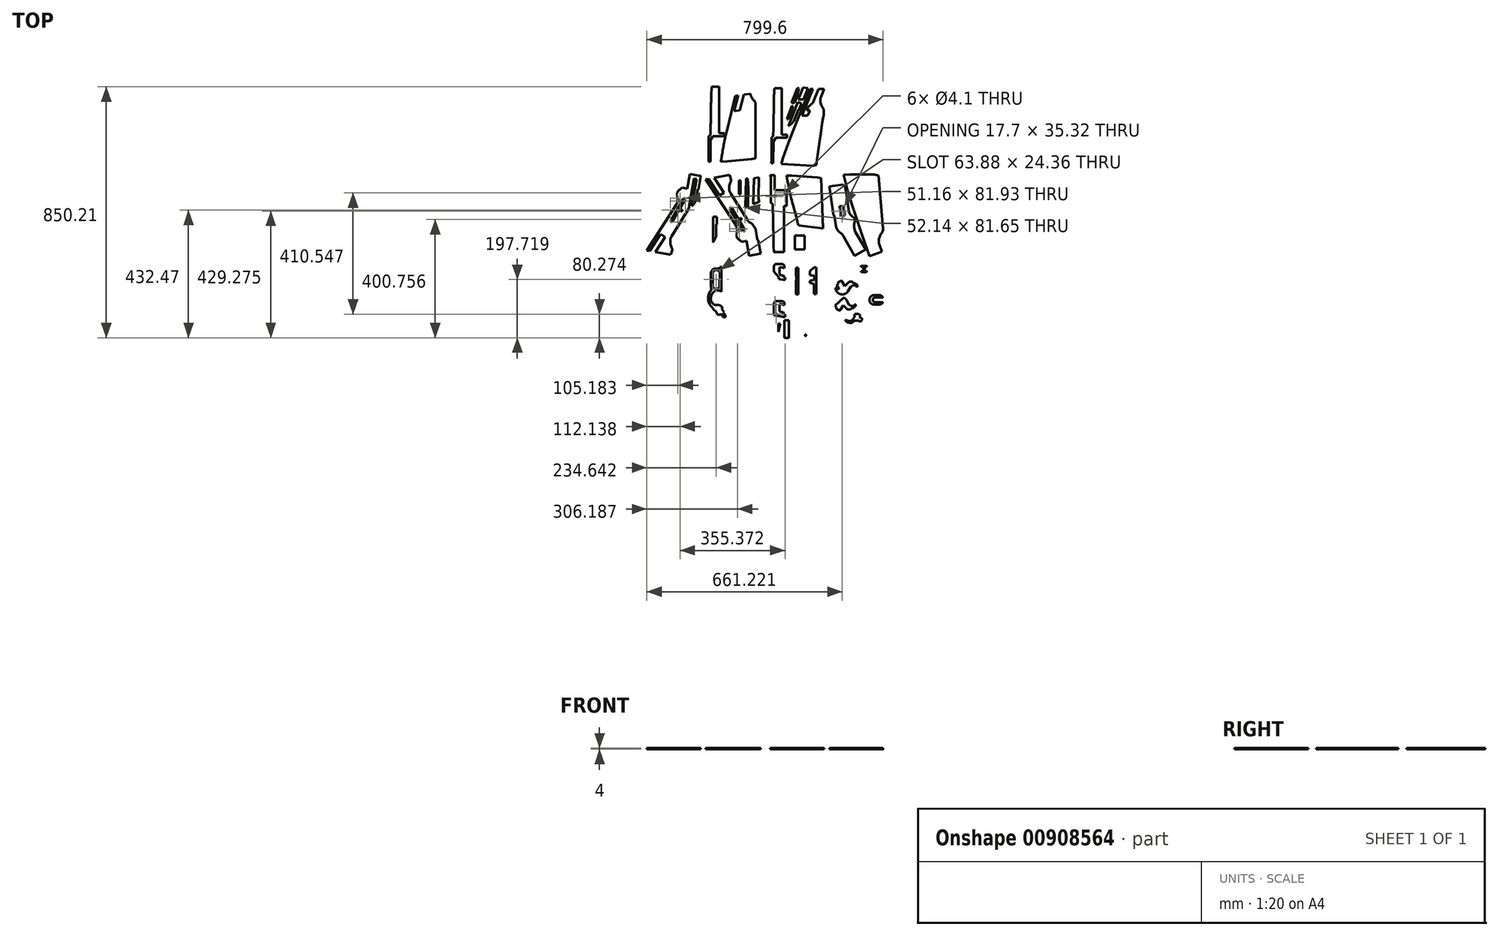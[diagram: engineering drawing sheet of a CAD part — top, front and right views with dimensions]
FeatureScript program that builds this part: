
annotation { "Feature Type Name" : "Feature", "Feature Type Description" : "" }
export const myFeature = defineFeature(function(context is Context, id is Id, definition is map)
    precondition{}
    {
        {
            var Q0;
            Q0=qCreatedBy(makeId("Top.planeOp"),FACE);
            var sketch = newSketch(context, id + "F0", { "sketchPlane" : qUnion([Q0])});
            skLineSegment(sketch, "E0", {"start": v(-149.17, 147.65) * mm, "end": v(-126.87, 148.64) * mm});
            skLineSegment(sketch, "E1", {"start": v(-126.87, 148.64) * mm, "end": v(-45.65, 148.64) * mm});
            skLineSegment(sketch, "E2", {"start": v(-45.65, 148.64) * mm, "end": v(-31.11, 145.65) * mm});
            skLineSegment(sketch, "E3", {"start": v(-31.11, 145.65) * mm, "end": v(-16.66, -19.3) * mm});
            skLineSegment(sketch, "E4", {"start": v(-149.17, 147.65) * mm, "end": v(-134.77, 92.63) * mm});
            skLineSegment(sketch, "E5", {"start": v(-134.77, 92.63) * mm, "end": v(-120.01, 43.25) * mm});
            skLineSegment(sketch, "E6", {"start": v(-120.01, 43.25) * mm, "end": v(-84.94, -59.33) * mm});
            skLineSegment(sketch, "E7", {"start": v(-84.94, -59.33) * mm, "end": v(-61, -127.23) * mm});
            skLineSegment(sketch, "E8", {"start": v(-61, -127.23) * mm, "end": v(-19.3, -112.53) * mm});
            skLineSegment(sketch, "E9", {"start": v(-19.3, -112.53) * mm, "end": v(-28.25, -87.13) * mm});
            skFitSpline(sketch, "E10", {"points": [v(-28.25, -87.13) * mm, v(-29.8, -80.26) * mm, v(-30, -73.96) * mm, v(-28.25, -65.46) * mm, v(-24.65, -56.16) * mm, v(-21.41, -51.03) * mm, v(-17.98, -46.65) * mm, v(-16.48, -43.2) * mm, v(-15.7, -38.91) * mm, v(-15.5, -33.52) * mm, v(-16.66, -19.3) * mm], "startDerivative": vector(-18, 68.99) * mm, "endDerivative": vector(-10.86, 110.65) * mm});
            skLineSegment(sketch, "E11", {"start": v(-196.66, 108.69) * mm, "end": v(-150.29, 115.09) * mm});
            skLineSegment(sketch, "E12", {"start": v(-150.29, 115.09) * mm, "end": v(-149.74, 111.15) * mm});
            skLineSegment(sketch, "E13", {"start": v(-196.66, 108.69) * mm, "end": v(-182.68, 10.6) * mm});
            skLineSegment(sketch, "E14", {"start": v(-182.68, 10.6) * mm, "end": v(-180.62, 10.89) * mm});
            skLineSegment(sketch, "E15", {"start": v(-180.62, 10.89) * mm, "end": v(-174.86, -29.47) * mm});
            skLineSegment(sketch, "E16", {"start": v(-174.86, -29.47) * mm, "end": v(-170.39, -37.35) * mm});
            skFitSpline(sketch, "E17", {"points": [v(-170.39, -37.35) * mm, v(-167.86, -41.24) * mm, v(-164.52, -45.04) * mm, v(-161.57, -47.92) * mm, v(-158, -49.98) * mm, v(-155.75, -51.53) * mm, v(-152.83, -54.2) * mm, v(-149.96, -58.52) * mm], "startDerivative": vector(15.54, -26.2) * mm, "endDerivative": vector(17.07, -29.01) * mm});
            skLineSegment(sketch, "E18", {"start": v(-149.96, -58.52) * mm, "end": v(-111.45, -126.79) * mm});
            skLineSegment(sketch, "E19", {"start": v(-111.45, -126.79) * mm, "end": v(-73.88, -104.23) * mm});
            skLineSegment(sketch, "E20", {"start": v(-73.88, -104.23) * mm, "end": v(-109.1, -45.56) * mm});
            skFitSpline(sketch, "E21", {"points": [v(-109.1, -45.56) * mm, v(-110.9, -40.12) * mm, v(-112.61, -33.86) * mm, v(-113.49, -27.7) * mm, v(-113.05, -20.62) * mm, v(-111.3, -12.06) * mm, v(-110.96, -7.06) * mm, v(-111.46, -2.22) * mm, v(-112.17, 0) * mm, v(-114.15, 2.77) * mm, v(-117.22, 5.63) * mm, v(-122.88, 9.97) * mm, v(-126.73, 13.7) * mm, v(-129.53, 18.43) * mm, v(-132.33, 32.32) * mm, v(-135.24, 52.15) * mm, v(-140.51, 88.4) * mm, v(-143.26, 106.36) * mm], "startDerivative": vector(-37.16, 108.53) * mm, "endDerivative": vector(-28.2, 180.9) * mm});
            skFitSpline(sketch, "E22", {"points": [v(-143.26, 106.36) * mm, v(-144.53, 106.7) * mm, v(-146.82, 107.98) * mm, v(-148.38, 109.32) * mm, v(-149.74, 111.15) * mm], "startDerivative": vector(-5.84, 1.08) * mm, "endDerivative": vector(-5.05, 7.35) * mm});
            skLineSegment(sketch, "E23", {"start": v(-162.7, 40.87) * mm, "end": v(-148.72, 42.74) * mm});
            skLineSegment(sketch, "E24.bottom", {"start": v(-314.34, -57.8) * mm, "end": v(-280.77, -57.8) * mm});
            skLineSegment(sketch, "E24.top", {"start": v(-314.34, -104.97) * mm, "end": v(-280.77, -104.97) * mm});
            skLineSegment(sketch, "E24.left", {"start": v(-314.34, -57.8) * mm, "end": v(-314.34, -104.97) * mm});
            skLineSegment(sketch, "E24.right", {"start": v(-280.77, -57.8) * mm, "end": v(-280.77, -104.97) * mm});
            skLineSegment(sketch, "E25", {"start": v(-383, 146.15) * mm, "end": v(-383, 95.33) * mm});
            skLineSegment(sketch, "E26", {"start": v(-383, 95.33) * mm, "end": v(-342.44, 95.33) * mm});
            skLineSegment(sketch, "E27", {"start": v(-342.44, 95.33) * mm, "end": v(-342.44, 43.12) * mm});
            skLineSegment(sketch, "E28", {"start": v(-342.44, 43.12) * mm, "end": v(-351.35, 43.12) * mm});
            skLineSegment(sketch, "E29", {"start": v(-351.35, 43.12) * mm, "end": v(-351.35, -114.1) * mm});
            skLineSegment(sketch, "E30", {"start": v(-351.35, -114.1) * mm, "end": v(-384.8, -114.1) * mm});
            skLineSegment(sketch, "E31", {"start": v(-384.8, -114.1) * mm, "end": v(-386.19, -93.06) * mm});
            skLineSegment(sketch, "E32", {"start": v(-386.19, -93.06) * mm, "end": v(-387.02, -71.35) * mm});
            skLineSegment(sketch, "E33", {"start": v(-383, 146.15) * mm, "end": v(-397.86, 146.15) * mm});
            skLineSegment(sketch, "E34", {"start": v(-395.25, 135.87) * mm, "end": v(-394.92, 52.8) * mm});
            skFitSpline(sketch, "E35", {"points": [v(-394.92, 52.8) * mm, v(-392.77, 51.57) * mm, v(-390.76, 49.56) * mm, v(-389.16, 47.04) * mm], "startDerivative": vector(6.95, -3.49) * mm, "endDerivative": vector(4.3, -7.5) * mm});
            skLineSegment(sketch, "E36", {"start": v(-389.16, 47.04) * mm, "end": v(-387.02, -71.35) * mm});
            skFitSpline(sketch, "E37", {"points": [v(-397.86, 146.15) * mm, v(-396.76, 144.34) * mm, v(-395.93, 141.6) * mm, v(-395.44, 139.07) * mm, v(-395.25, 135.87) * mm], "startDerivative": vector(5.35, -7.46) * mm, "endDerivative": vector(0.37, -12.14) * mm});
            skLineSegment(sketch, "E38", {"start": v(-301.57, -24.08) * mm, "end": v(-219.1, -33.52) * mm});
            skLineSegment(sketch, "E39", {"start": v(-219.1, -33.52) * mm, "end": v(-224.66, 136.63) * mm});
            skLineSegment(sketch, "E40", {"start": v(-224.66, 136.63) * mm, "end": v(-237.68, 139.4) * mm});
            skLineSegment(sketch, "E41", {"start": v(-237.68, 139.4) * mm, "end": v(-325.29, 144.76) * mm});
            skLineSegment(sketch, "E42", {"start": v(-325.29, 144.76) * mm, "end": v(-342.06, 144.76) * mm});
            skFitSpline(sketch, "E43", {"points": [v(-342.06, 144.76) * mm, v(-331.72, 90.05) * mm, v(-321.47, 49.6) * mm, v(-304.84, -11.83) * mm, v(-301.57, -24.08) * mm], "startDerivative": vector(35.43, -199.62) * mm, "endDerivative": vector(17.76, -66.84) * mm});
            skCircle(sketch, "E44", {"center": v(-381.6, 74.58) * mm, "radius": 2.05 * mm});
            skPoint(sketch, "E44.first.point", {"position": v(-383.07, 76) * mm});
            skPoint(sketch, "E44.second.point", {"position": v(-380.17, 73.1) * mm});
            skPoint(sketch, "E44.third.point", {"position": v(-379.55, 74.67) * mm});
            skCircle(sketch, "E45", {"center": v(-347.56, 86.62) * mm, "radius": 2.05 * mm});
            skPoint(sketch, "E45.first.point", {"position": v(-349.02, 85.18) * mm});
            skPoint(sketch, "E45.second.point", {"position": v(-348.67, 88.34) * mm});
            skPoint(sketch, "E45.third.point", {"position": v(-346.2, 85.1) * mm});
            skLineSegment(sketch, "E46.bottom", {"start": v(-503.4, 129.01) * mm, "end": v(-497.69, 129.01) * mm});
            skLineSegment(sketch, "E46.top", {"start": v(-503.4, 81.78) * mm, "end": v(-497.69, 81.78) * mm});
            skLineSegment(sketch, "E46.left", {"start": v(-503.4, 129.01) * mm, "end": v(-503.4, 81.78) * mm});
            skLineSegment(sketch, "E46.right", {"start": v(-497.69, 129.01) * mm, "end": v(-497.69, 81.78) * mm});
            skLineSegment(sketch, "E47.bottom", {"start": v(-591.28, 5.95) * mm, "end": v(-580.52, 5.95) * mm});
            skLineSegment(sketch, "E47.left", {"start": v(-591.28, 5.95) * mm, "end": v(-591.28, -60.08) * mm});
            skLineSegment(sketch, "E47.right", {"start": v(-580.52, -19.16) * mm, "end": v(-580.52, -60.08) * mm});
            skLineSegment(sketch, "E48.bottom", {"start": v(-580.52, 5.95) * mm, "end": v(-578.75, 5.95) * mm});
            skLineSegment(sketch, "E48.top", {"start": v(-580.52, -19.16) * mm, "end": v(-578.75, -19.16) * mm});
            skLineSegment(sketch, "E48.right", {"start": v(-578.75, 5.95) * mm, "end": v(-578.75, -19.16) * mm});
            skLineSegment(sketch, "E49", {"start": v(-591.28, -60.08) * mm, "end": v(-591.28, -80.06) * mm});
            skFitSpline(sketch, "E50", {"points": [v(-591.28, -80.06) * mm, v(-589.15, -77.9) * mm, v(-585.89, -72.42) * mm, v(-584.72, -69.68) * mm, v(-582.39, -64.6) * mm, v(-580.52, -60.08) * mm], "startDerivative": vector(12.22, 10.36) * mm, "endDerivative": vector(8.13, 20.7) * mm});
            skLineSegment(sketch, "E51", {"start": v(-452.11, 136.32) * mm, "end": v(-435.67, 139.35) * mm});
            skLineSegment(sketch, "E52", {"start": v(-435.67, 139.35) * mm, "end": v(-436.72, 68.57) * mm});
            skLineSegment(sketch, "E53", {"start": v(-454.8, 48.27) * mm, "end": v(-452.11, 136.32) * mm});
            skLineSegment(sketch, "E54", {"start": v(-479.29, 134.92) * mm, "end": v(-474.5, 134.92) * mm});
            skLineSegment(sketch, "E55", {"start": v(-474.5, 134.92) * mm, "end": v(-471, 101.92) * mm});
            skLineSegment(sketch, "E56", {"start": v(-471, 101.92) * mm, "end": v(-473.1, 41.16) * mm});
            skLineSegment(sketch, "E57", {"start": v(-473.1, 41.16) * mm, "end": v(-482.09, 37.31) * mm});
            skLineSegment(sketch, "E58", {"start": v(-482.09, 37.31) * mm, "end": v(-479.29, 134.92) * mm});
            skLineSegment(sketch, "E59", {"start": v(-454.8, 48.27) * mm, "end": v(-434.27, 56.1) * mm});
            skFitSpline(sketch, "E60", {"points": [v(-436.72, 68.57) * mm, v(-436.47, 64.62) * mm, v(-435.57, 59.76) * mm, v(-434.27, 56.1) * mm], "startDerivative": vector(0.43, -11.83) * mm, "endDerivative": vector(4.36, -10.9) * mm});
            skLineSegment(sketch, "E61", {"start": v(-534.95, 33.65) * mm, "end": v(-528.54, 37.38) * mm});
            skLineSegment(sketch, "E62", {"start": v(-528.54, 37.38) * mm, "end": v(-482.81, -40.18) * mm});
            skLineSegment(sketch, "E63", {"start": v(-482.81, -40.18) * mm, "end": v(-489.2, -44.27) * mm});
            skLineSegment(sketch, "E64", {"start": v(-489.2, -44.27) * mm, "end": v(-534.95, 33.65) * mm});
            skLineSegment(sketch, "E65", {"start": v(-616.2, 132.06) * mm, "end": v(-606.63, 133.87) * mm});
            skLineSegment(sketch, "E66", {"start": v(-587.47, 137.5) * mm, "end": v(-554.17, 87.16) * mm});
            skLineSegment(sketch, "E67", {"start": v(-554.17, 87.16) * mm, "end": v(-568.87, 77.44) * mm});
            skLineSegment(sketch, "E68", {"start": v(-568.87, 77.44) * mm, "end": v(-606.63, 133.87) * mm});
            skLineSegment(sketch, "E69.trimOffspring", {"start": v(-587.47, 137.5) * mm, "end": v(-534.95, 147.45) * mm});
            skLineSegment(sketch, "E70", {"start": v(-616.2, 132.06) * mm, "end": v(-514.72, -20.8) * mm});
            skLineSegment(sketch, "E71", {"start": v(-493.99, -79.22) * mm, "end": v(-478.24, -76.24) * mm});
            skLineSegment(sketch, "E72", {"start": v(-478.24, -76.24) * mm, "end": v(-468.8, -126.1) * mm});
            skLineSegment(sketch, "E73", {"start": v(-468.8, -126.1) * mm, "end": v(-429.68, -118.69) * mm});
            skLineSegment(sketch, "E74", {"start": v(-429.68, -118.69) * mm, "end": v(-438.3, -73.19) * mm});
            skLineSegment(sketch, "E75", {"start": v(-438.3, -73.19) * mm, "end": v(-440.32, -73.57) * mm});
            skLineSegment(sketch, "E76", {"start": v(-440.32, -73.57) * mm, "end": v(-447.9, -33.57) * mm});
            skFitSpline(sketch, "E77", {"points": [v(-514.72, -20.8) * mm, v(-511.56, -28.47) * mm, v(-510.2, -33.46) * mm, v(-509.34, -38.57) * mm, v(-509.26, -43.03) * mm, v(-509.91, -48.3) * mm, v(-510.82, -55.6) * mm, v(-510.62, -61.75) * mm, v(-509.13, -66.28) * mm, v(-505.05, -70.7) * mm, v(-499.15, -74.82) * mm, v(-493.99, -79.22) * mm], "startDerivative": vector(33.2, -75.83) * mm, "endDerivative": vector(51.36, -47.06) * mm});
            skFitSpline(sketch, "E78", {"points": [v(-447.9, -33.57) * mm, v(-455.6, -22.09) * mm, v(-460.73, -16.75) * mm, v(-464.6, -14.46) * mm, v(-467.8, -12.8) * mm, v(-471.54, -9.6) * mm, v(-474.18, -5.93) * mm], "startDerivative": vector(-31.47, 49.76) * mm, "endDerivative": vector(-16.54, 26.08) * mm});
            skLineSegment(sketch, "E79", {"start": v(-474.18, -5.93) * mm, "end": v(-531.19, 84.12) * mm});
            skFitSpline(sketch, "E80", {"points": [v(-531.19, 84.12) * mm, v(-533.78, 89.12) * mm, v(-535.65, 94.17) * mm, v(-536.33, 99.42) * mm, v(-536.48, 104.86) * mm, v(-535.94, 110.6) * mm, v(-533.93, 118.6) * mm, v(-531.97, 123.5) * mm, v(-531.19, 125.36) * mm, v(-530.5, 127.17) * mm, v(-530.35, 130.16) * mm, v(-531.19, 136.49) * mm, v(-534.95, 147.45) * mm], "startDerivative": vector(-31.22, 57.32) * mm, "endDerivative": vector(-36.04, 92.43) * mm});
            skCircle(sketch, "E81", {"center": v(-497.57, -2.3) * mm, "radius": 3.05 * mm});
            skCircle(sketch, "E82", {"center": v(-501.46, -34.62) * mm, "radius": 2.05 * mm});
            skLineSegment(sketch, "E83", {"start": v(-595.8, 446) * mm, "end": v(-570.14, 446) * mm});
            skLineSegment(sketch, "E84", {"start": v(-570.14, 446) * mm, "end": v(-570.14, 288.85) * mm});
            skLineSegment(sketch, "E85", {"start": v(-570.14, 288.85) * mm, "end": v(-553.29, 288.85) * mm});
            skLineSegment(sketch, "E86", {"start": v(-553.29, 288.85) * mm, "end": v(-553.29, 278.65) * mm});
            skLineSegment(sketch, "E87", {"start": v(-553.29, 278.65) * mm, "end": v(-591.63, 278.65) * mm});
            skLineSegment(sketch, "E88", {"start": v(-591.63, 278.65) * mm, "end": v(-599.38, 266.2) * mm});
            skLineSegment(sketch, "E89", {"start": v(-599.38, 266.2) * mm, "end": v(-600.1, 191.95) * mm});
            skLineSegment(sketch, "E90", {"start": v(-600.1, 191.95) * mm, "end": v(-606.46, 191.95) * mm});
            skLineSegment(sketch, "E91", {"start": v(-606.46, 191.95) * mm, "end": v(-606.23, 194.56) * mm});
            skLineSegment(sketch, "E92", {"start": v(-606.23, 194.56) * mm, "end": v(-606.08, 197.13) * mm});
            skLineSegment(sketch, "E93", {"start": v(-606.08, 197.13) * mm, "end": v(-606.08, 200.1) * mm});
            skLineSegment(sketch, "E94", {"start": v(-606.08, 200.1) * mm, "end": v(-605.64, 278.92) * mm});
            skFitSpline(sketch, "E95", {"points": [v(-605.64, 278.92) * mm, v(-604.04, 279.9) * mm, v(-602.52, 281.19) * mm, v(-600.71, 283.34) * mm, v(-599.96, 284.63) * mm], "startDerivative": vector(6.84, 3.95) * mm, "endDerivative": vector(2.92, 5.54) * mm});
            skFitSpline(sketch, "E96", {"points": [v(-599.96, 284.63) * mm, v(-599.55, 302.7) * mm, v(-598.96, 321.54) * mm, v(-598.26, 367.43) * mm, v(-597.86, 393.38) * mm, v(-597.68, 403.88) * mm, v(-595.8, 446) * mm], "startDerivative": vector(2.54, 132.3) * mm, "endDerivative": vector(11.3, 232.58) * mm});
            skLineSegment(sketch, "E97", {"start": v(-515.51, 415.22) * mm, "end": v(-505.83, 416.56) * mm});
            skLineSegment(sketch, "E98", {"start": v(-486.33, 419.24) * mm, "end": v(-500.24, 366.83) * mm});
            skLineSegment(sketch, "E99", {"start": v(-500.24, 366.83) * mm, "end": v(-519.5, 364.17) * mm});
            skLineSegment(sketch, "E100", {"start": v(-519.5, 364.17) * mm, "end": v(-505.83, 416.56) * mm});
            skLineSegment(sketch, "E101.trimOffspring", {"start": v(-486.33, 419.24) * mm, "end": v(-464.67, 422.22) * mm});
            skLineSegment(sketch, "E102", {"start": v(-515.51, 415.22) * mm, "end": v(-544.43, 298.33) * mm});
            skFitSpline(sketch, "E103", {"points": [v(-544.43, 298.33) * mm, v(-550.49, 272.31) * mm, v(-555, 249.75) * mm, v(-561.08, 214.25) * mm, v(-564.41, 192.48) * mm], "startDerivative": vector(-25.75, -108.04) * mm, "endDerivative": vector(-13, -87.66) * mm});
            skLineSegment(sketch, "E104", {"start": v(-564.41, 192.48) * mm, "end": v(-542, 193.7) * mm});
            skLineSegment(sketch, "E105", {"start": v(-542, 193.7) * mm, "end": v(-460.2, 201.02) * mm});
            skLineSegment(sketch, "E106", {"start": v(-460.2, 201.02) * mm, "end": v(-447.26, 204.35) * mm});
            skLineSegment(sketch, "E107", {"start": v(-447.26, 204.35) * mm, "end": v(-446.92, 383.54) * mm});
            skFitSpline(sketch, "E108", {"points": [v(-464.67, 422.22) * mm, v(-463.67, 418.16) * mm, v(-461.6, 412.63) * mm, v(-458.85, 407.56) * mm, v(-454.15, 400.88) * mm, v(-450.43, 397.13) * mm, v(-448.74, 394.32) * mm, v(-447.42, 389.13) * mm, v(-446.92, 383.54) * mm], "startDerivative": vector(7.6, -35.17) * mm, "endDerivative": vector(2.42, -43.3) * mm});
            skLineSegment(sketch, "E109", {"start": v(-285.96, 444.07) * mm, "end": v(-269.63, 440.77) * mm});
            skLineSegment(sketch, "E110", {"start": v(-269.63, 440.77) * mm, "end": v(-284.72, 402.76) * mm});
            skLineSegment(sketch, "E111", {"start": v(-284.72, 402.76) * mm, "end": v(-303.2, 402.76) * mm});
            skLineSegment(sketch, "E112", {"start": v(-303.2, 402.76) * mm, "end": v(-285.96, 444.07) * mm});
            skLineSegment(sketch, "E113", {"start": v(-305, 441.93) * mm, "end": v(-300.64, 439.78) * mm});
            skLineSegment(sketch, "E114", {"start": v(-300.64, 439.78) * mm, "end": v(-309.3, 407.87) * mm});
            skLineSegment(sketch, "E115", {"start": v(-309.3, 407.87) * mm, "end": v(-315.73, 391.7) * mm});
            skLineSegment(sketch, "E116", {"start": v(-315.73, 391.7) * mm, "end": v(-325.87, 391.7) * mm});
            skLineSegment(sketch, "E117", {"start": v(-325.87, 391.7) * mm, "end": v(-305, 441.93) * mm});
            skLineSegment(sketch, "E118", {"start": v(-262.54, 438.88) * mm, "end": v(-252.64, 438.88) * mm});
            skLineSegment(sketch, "E119", {"start": v(-252.64, 438.88) * mm, "end": v(-290.2, 349.15) * mm});
            skLineSegment(sketch, "E120", {"start": v(-290.2, 349.15) * mm, "end": v(-271.2, 349.15) * mm});
            skLineSegment(sketch, "E121", {"start": v(-271.2, 349.15) * mm, "end": v(-265.1, 363.05) * mm});
            skLineSegment(sketch, "E122", {"start": v(-273.74, 366.84) * mm, "end": v(-269.37, 377.54) * mm});
            skLineSegment(sketch, "E123", {"start": v(-269.37, 377.54) * mm, "end": v(-252.67, 392.24) * mm});
            skLineSegment(sketch, "E124", {"start": v(-252.67, 392.24) * mm, "end": v(-233.62, 438.58) * mm});
            skLineSegment(sketch, "E125", {"start": v(-233.62, 438.58) * mm, "end": v(-215.07, 438.58) * mm});
            skLineSegment(sketch, "E126", {"start": v(-215.07, 438.58) * mm, "end": v(-223.89, 416.23) * mm});
            skArc(sketch, "E127", {"start": v(-265.1, 363.05) * mm, "mid": v(-266.87, 367.6) * mm, "end": v(-271.42, 365.82) * mm});
            skLineSegment(sketch, "E128.trimOffspring", {"start": v(-271.42, 365.82) * mm, "end": v(-273.74, 366.84) * mm});
            skFitSpline(sketch, "E129", {"points": [v(-223.89, 416.23) * mm, v(-226.3, 409.8) * mm, v(-227.65, 404.36) * mm, v(-227.9, 399.57) * mm, v(-227.44, 394.38) * mm, v(-226.04, 387.5) * mm, v(-223.16, 380.44) * mm, v(-219.78, 374.92) * mm, v(-217.34, 371.37) * mm, v(-216.06, 367.62) * mm, v(-215.7, 362.59) * mm, v(-215.78, 358.26) * mm, v(-219.12, 336.12) * mm, v(-241.66, 180.43) * mm], "startDerivative": vector(-42.3, -107.3) * mm, "endDerivative": vector(-91.6, -646.22) * mm});
            skLineSegment(sketch, "E130", {"start": v(-241.66, 180.43) * mm, "end": v(-253.53, 178.88) * mm});
            skLineSegment(sketch, "E131", {"start": v(-253.53, 178.88) * mm, "end": v(-337.8, 183.45) * mm});
            skLineSegment(sketch, "E132", {"start": v(-337.8, 183.45) * mm, "end": v(-359.57, 185.32) * mm});
            skLineSegment(sketch, "E133", {"start": v(-359.57, 185.32) * mm, "end": v(-354.14, 203.4) * mm});
            skLineSegment(sketch, "E134", {"start": v(-354.14, 203.4) * mm, "end": v(-336.1, 257.34) * mm});
            skLineSegment(sketch, "E135", {"start": v(-336.1, 257.34) * mm, "end": v(-321, 296.18) * mm});
            skLineSegment(sketch, "E136", {"start": v(-321, 296.18) * mm, "end": v(-297.96, 353.69) * mm});
            skLineSegment(sketch, "E137", {"start": v(-297.96, 353.69) * mm, "end": v(-262.54, 438.88) * mm});
            skLineSegment(sketch, "E138", {"start": v(-340.38, 337.3) * mm, "end": v(-336, 335.66) * mm});
            skLineSegment(sketch, "E139", {"start": v(-336, 335.66) * mm, "end": v(-320.42, 379.94) * mm});
            skLineSegment(sketch, "E140", {"start": v(-320.42, 379.94) * mm, "end": v(-324.68, 381.44) * mm});
            skLineSegment(sketch, "E141", {"start": v(-324.68, 381.44) * mm, "end": v(-340.38, 337.3) * mm});
            skLineSegment(sketch, "E142", {"start": v(-303.35, 394.01) * mm, "end": v(-291.74, 389.75) * mm});
            skPoint(sketch, "E142.startSnap0", {"position": v(-271.42, 394.01) * mm});
            skLineSegment(sketch, "E143", {"start": v(-291.74, 389.75) * mm, "end": v(-300.88, 366.49) * mm});
            skLineSegment(sketch, "E144", {"start": v(-300.88, 366.49) * mm, "end": v(-302.68, 367.2) * mm});
            skLineSegment(sketch, "E145", {"start": v(-302.68, 367.2) * mm, "end": v(-317.7, 329.47) * mm});
            skLineSegment(sketch, "E146", {"start": v(-303.35, 394.01) * mm, "end": v(-335.17, 314.4) * mm});
            skFitSpline(sketch, "E147", {"points": [v(-335.17, 314.4) * mm, v(-332.05, 315.96) * mm, v(-326.93, 319.65) * mm, v(-322.2, 324.58) * mm, v(-317.7, 329.47) * mm], "startDerivative": vector(15.06, 6.83) * mm, "endDerivative": vector(16.78, 18.03) * mm});
            skLineSegment(sketch, "E148", {"start": v(-394, 187.22) * mm, "end": v(-387.43, 187.22) * mm});
            skLineSegment(sketch, "E149", {"start": v(-387.43, 187.22) * mm, "end": v(-387, 261.25) * mm});
            skLineSegment(sketch, "E150", {"start": v(-387, 261.25) * mm, "end": v(-379.3, 274.15) * mm});
            skLineSegment(sketch, "E151", {"start": v(-379.3, 274.15) * mm, "end": v(-340.63, 274.15) * mm});
            skLineSegment(sketch, "E152", {"start": v(-340.63, 274.15) * mm, "end": v(-340.63, 284.1) * mm});
            skLineSegment(sketch, "E153", {"start": v(-340.63, 284.1) * mm, "end": v(-358.53, 284.1) * mm});
            skLineSegment(sketch, "E154", {"start": v(-358.53, 284.1) * mm, "end": v(-358.53, 441.29) * mm});
            skLineSegment(sketch, "E155", {"start": v(-358.53, 441.29) * mm, "end": v(-383.06, 441.29) * mm});
            skFitSpline(sketch, "E156", {"points": [v(-383.06, 441.29) * mm, v(-383.6, 431.27) * mm, v(-384.23, 422.85) * mm, v(-384.64, 414.84) * mm, v(-385.03, 398.61) * mm, v(-385.55, 371.36) * mm, v(-385.82, 344.35) * mm, v(-386.34, 316.13) * mm, v(-387.1, 287.59) * mm, v(-387.28, 280.07) * mm], "startDerivative": vector(-5.75, -118.16) * mm, "endDerivative": vector(-1.72, -83.06) * mm});
            skFitSpline(sketch, "E157", {"points": [v(-387.28, 280.07) * mm, v(-388.46, 278.37) * mm, v(-389.24, 277.4) * mm, v(-390.77, 275.94) * mm, v(-393.04, 274.37) * mm], "startDerivative": vector(-4.95, -7.29) * mm, "endDerivative": vector(-8.06, -5.16) * mm});
            skLineSegment(sketch, "E158", {"start": v(-393.04, 274.37) * mm, "end": v(-393.35, 191.7) * mm});
            skFitSpline(sketch, "E159", {"points": [v(-394, 187.22) * mm, v(-393.66, 188.73) * mm, v(-393.35, 191.7) * mm], "startDerivative": vector(0.87, 3.29) * mm, "endDerivative": vector(0.45, 5.56) * mm});
            skLineSegment(sketch, "E160", {"start": v(-696.03, 104.4) * mm, "end": v(-678.42, 100.9) * mm});
            skLineSegment(sketch, "E161", {"start": v(-678.42, 100.9) * mm, "end": v(-669.6, 150.83) * mm});
            skLineSegment(sketch, "E162", {"start": v(-669.6, 150.83) * mm, "end": v(-632.31, 144.24) * mm});
            skLineSegment(sketch, "E163", {"start": v(-632.31, 144.24) * mm, "end": v(-640.34, 98.84) * mm});
            skLineSegment(sketch, "E164", {"start": v(-640.34, 98.84) * mm, "end": v(-642.45, 99.22) * mm});
            skLineSegment(sketch, "E165", {"start": v(-642.45, 99.22) * mm, "end": v(-649.51, 59.3) * mm});
            skLineSegment(sketch, "E166", {"start": v(-663.57, 41.2) * mm, "end": v(-647, 133.86) * mm});
            skLineSegment(sketch, "E167", {"start": v(-647, 133.86) * mm, "end": v(-655.42, 135.36) * mm});
            skLineSegment(sketch, "E168", {"start": v(-655.42, 135.36) * mm, "end": v(-673.55, 34) * mm});
            skLineSegment(sketch, "E169", {"start": v(-673.55, 34) * mm, "end": v(-730.28, -58.76) * mm});
            skLineSegment(sketch, "E170", {"start": v(-733.93, -123.22) * mm, "end": v(-786.63, -113.85) * mm});
            skLineSegment(sketch, "E171", {"start": v(-815.07, -108.8) * mm, "end": v(-716.09, 45.38) * mm});
            skLineSegment(sketch, "E172", {"start": v(-690.84, 69.23) * mm, "end": v(-684.3, 65.38) * mm});
            skLineSegment(sketch, "E173", {"start": v(-684.3, 65.38) * mm, "end": v(-728.92, -12.7) * mm});
            skLineSegment(sketch, "E174", {"start": v(-728.92, -12.7) * mm, "end": v(-735.47, -8.95) * mm});
            skLineSegment(sketch, "E175", {"start": v(-735.47, -8.95) * mm, "end": v(-690.84, 69.23) * mm});
            skLineSegment(sketch, "E176", {"start": v(-805.86, -110.43) * mm, "end": v(-768.85, -53.23) * mm});
            skLineSegment(sketch, "E177", {"start": v(-768.85, -53.23) * mm, "end": v(-753.73, -63) * mm});
            skLineSegment(sketch, "E178", {"start": v(-753.73, -63) * mm, "end": v(-786.63, -113.85) * mm});
            skLineSegment(sketch, "E179.trimOffspring", {"start": v(-805.86, -110.43) * mm, "end": v(-815.07, -108.8) * mm});
            skFitSpline(sketch, "E180", {"points": [v(-663.57, 41.2) * mm, v(-660.75, 43.5) * mm, v(-656.73, 47.7) * mm, v(-653.52, 52.6) * mm, v(-651.89, 55.34) * mm, v(-649.51, 59.3) * mm], "startDerivative": vector(15.14, 11.8) * mm, "endDerivative": vector(12.6, 20.94) * mm});
            skFitSpline(sketch, "E181", {"points": [v(-730.28, -58.76) * mm, v(-732.26, -62.15) * mm, v(-733.93, -65.15) * mm, v(-735.4, -70) * mm, v(-735.99, -75.64) * mm, v(-736.08, -81.72) * mm, v(-734.71, -89.22) * mm, v(-732.01, -97.6) * mm, v(-730.28, -101.48) * mm, v(-729.41, -105.45) * mm, v(-730.28, -111.48) * mm, v(-733.93, -123.22) * mm], "startDerivative": vector(-27.19, -47.28) * mm, "endDerivative": vector(-31.95, -95.99) * mm});
            skFitSpline(sketch, "E182", {"points": [v(-716.09, 45.38) * mm, v(-713.3, 51.62) * mm, v(-711.95, 56.43) * mm, v(-710.67, 65) * mm, v(-711.26, 71.53) * mm, v(-712.48, 78.06) * mm, v(-712.65, 84.7) * mm, v(-710.96, 91.41) * mm, v(-706.77, 95.79) * mm, v(-702.22, 99) * mm, v(-696.03, 104.4) * mm], "startDerivative": vector(28.1, 45.56) * mm, "endDerivative": vector(57.44, 53.16) * mm});
            skCircle(sketch, "E183", {"center": v(-702.93, 59.44) * mm, "radius": 2.05 * mm});
            skCircle(sketch, "E184", {"center": v(-698.54, 27.39) * mm, "radius": 3.05 * mm});
            skLineSegment(sketch, "E185", {"start": v(-565.61, -163.44) * mm, "end": v(-562.9, -163.44) * mm});
            skLineSegment(sketch, "E186", {"start": v(-562.9, -163.44) * mm, "end": v(-562.9, -248.77) * mm});
            skLineSegment(sketch, "E187", {"start": v(-581.22, -238.42) * mm, "end": v(-580.38, -174.54) * mm, "construction": true});
            skArc(sketch, "E188", {"start": v(-568.25, -185.04) * mm, "mid": v(-580.23, -174.54) * mm, "end": v(-592.1, -185.16) * mm});
            skArc(sketch, "E189", {"start": v(-592.6, -229.14) * mm, "mid": v(-580.67, -238.42) * mm, "end": v(-569.06, -228.72) * mm});
            skLineSegment(sketch, "E190", {"start": v(-592.1, -185.16) * mm, "end": v(-592.6, -229.14) * mm});
            skLineSegment(sketch, "E191", {"start": v(-568.25, -185.04) * mm, "end": v(-569.06, -228.72) * mm});
            skLineSegment(sketch, "E192", {"start": v(-598.89, -230.01) * mm, "end": v(-598.36, -185.16) * mm});
            skLineSegment(sketch, "E193", {"start": v(-562.45, -323.76) * mm, "end": v(-556, -333.56) * mm});
            skLineSegment(sketch, "E194", {"start": v(-551.85, -334.42) * mm, "end": v(-549.91, -333.14) * mm});
            skLineSegment(sketch, "E195", {"start": v(-549.1, -328.91) * mm, "end": v(-556.57, -318.32) * mm});
            skLineSegment(sketch, "E196", {"start": v(-556.57, -318.32) * mm, "end": v(-554.5, -316.87) * mm});
            skLineSegment(sketch, "E197", {"start": v(-554.5, -316.87) * mm, "end": v(-560.71, -308.06) * mm});
            skPoint(sketch, "E198.visualSharp", {"position": v(-547.33, -331.44) * mm});
            skArc(sketch, "E198.filletArc", {"start": v(-549.91, -333.14) * mm, "mid": v(-548.61, -331.2) * mm, "end": v(-549.1, -328.91) * mm});
            skPoint(sketch, "E199.visualSharp", {"position": v(-554.36, -336.07) * mm});
            skArc(sketch, "E199.filletArc", {"start": v(-556, -333.56) * mm, "mid": v(-554.1, -334.85) * mm, "end": v(-551.85, -334.42) * mm});
            skFitSpline(sketch, "E200", {"points": [v(-598.36, -185.16) * mm, v(-597.65, -182.33) * mm, v(-596.02, -178.55) * mm, v(-593.6, -174.84) * mm, v(-591.17, -172.59) * mm, v(-589.33, -171.4) * mm, v(-585.97, -169.85) * mm, v(-582.4, -169.09) * mm, v(-579.87, -168.98) * mm, v(-576.95, -169.33) * mm, v(-574.04, -169.68) * mm, v(-571.79, -169.47) * mm, v(-569.95, -168.4) * mm, v(-567.66, -166.49) * mm, v(-565.61, -163.44) * mm], "startDerivative": vector(8.21, 39.49) * mm, "endDerivative": vector(24.32, 41.97) * mm});
            skFitSpline(sketch, "E201", {"points": [v(-577.37, -324.78) * mm, v(-573.83, -325.6) * mm, v(-570.07, -325.65) * mm, v(-566.07, -325.16) * mm, v(-562.45, -323.76) * mm], "startDerivative": vector(14.43, -4.15) * mm, "endDerivative": vector(14.05, 6.4) * mm});
            skFitSpline(sketch, "E202", {"points": [v(-562.9, -248.77) * mm, v(-564.89, -246.97) * mm, v(-569, -244.47) * mm, v(-573.32, -243.34) * mm, v(-577.59, -243.05) * mm, v(-581.9, -244.13) * mm, v(-585.48, -246.09) * mm, v(-588.57, -248.15) * mm, v(-592.89, -251.87) * mm, v(-596.86, -259.18) * mm, v(-598.36, -267.96) * mm, v(-598.92, -272.47) * mm, v(-598.36, -277.76) * mm, v(-595.17, -284.58) * mm, v(-591.5, -289.33) * mm, v(-587.6, -291.74) * mm, v(-582.23, -292.96) * mm, v(-574.73, -293.18) * mm, v(-569.82, -293.3) * mm, v(-565.39, -294.85) * mm, v(-562.27, -297.5) * mm, v(-560.31, -302) * mm, v(-560.19, -304.56) * mm, v(-560.71, -308.06) * mm], "startDerivative": vector(-55.16, 54.11) * mm, "endDerivative": vector(-17.32, -101.28) * mm});
            skFitSpline(sketch, "E203", {"points": [v(-598.89, -230.01) * mm, v(-597.9, -231.75) * mm, v(-596.86, -233.98) * mm, v(-596.58, -236.82) * mm, v(-596.64, -239.15) * mm, v(-597.5, -241.98) * mm, v(-598.67, -244.25) * mm, v(-600.23, -246.3) * mm, v(-601.9, -248.77) * mm, v(-604.32, -253.59) * mm, v(-606.75, -260.85) * mm, v(-607.4, -265.17) * mm, v(-607.68, -272.09) * mm, v(-606.7, -279.92) * mm, v(-603.55, -288.84) * mm, v(-598.89, -296.3) * mm, v(-594.47, -301.91) * mm, v(-591.54, -305.76) * mm, v(-587.87, -309.8) * mm, v(-584.46, -312.5) * mm, v(-580.71, -315.86) * mm, v(-578.38, -319.36) * mm, v(-577.64, -321.96) * mm, v(-577.37, -324.78) * mm], "startDerivative": vector(32.78, -58.19) * mm, "endDerivative": vector(5.43, -83.01) * mm});
            skLineSegment(sketch, "E204", {"start": v(-249.5, -256.06) * mm, "end": v(-241.6, -256.06) * mm});
            skLineSegment(sketch, "E205", {"start": v(-241.6, -256.06) * mm, "end": v(-241.6, -165.9) * mm});
            skLineSegment(sketch, "E206", {"start": v(-241.6, -165.9) * mm, "end": v(-249.78, -165.9) * mm});
            skLineSegment(sketch, "E207", {"start": v(-249.78, -165.9) * mm, "end": v(-262.81, -178.4) * mm});
            skLineSegment(sketch, "E208", {"start": v(-262.81, -178.4) * mm, "end": v(-262.81, -190.6) * mm});
            skLineSegment(sketch, "E209", {"start": v(-262.81, -190.6) * mm, "end": v(-259.2, -191.98) * mm});
            skLineSegment(sketch, "E210", {"start": v(-259.2, -191.98) * mm, "end": v(-248.39, -194.2) * mm});
            skLineSegment(sketch, "E211", {"start": v(-248.39, -194.2) * mm, "end": v(-248.39, -208.2) * mm});
            skLineSegment(sketch, "E212", {"start": v(-248.39, -208.2) * mm, "end": v(-259.07, -210.7) * mm});
            skLineSegment(sketch, "E213", {"start": v(-259.07, -210.7) * mm, "end": v(-262.81, -211.81) * mm});
            skLineSegment(sketch, "E214", {"start": v(-262.81, -211.81) * mm, "end": v(-262.81, -218.06) * mm});
            skLineSegment(sketch, "E215", {"start": v(-262.81, -218.06) * mm, "end": v(-249.36, -221.1) * mm});
            skLineSegment(sketch, "E216", {"start": v(-249.36, -221.1) * mm, "end": v(-249.5, -256.06) * mm});
            skLineSegment(sketch, "E217.bottom", {"start": v(-350.05, -345.17) * mm, "end": v(-334.07, -345.17) * mm});
            skLineSegment(sketch, "E217.top", {"start": v(-350.05, -404.2) * mm, "end": v(-334.07, -404.2) * mm});
            skLineSegment(sketch, "E217.left", {"start": v(-350.05, -345.17) * mm, "end": v(-350.05, -404.2) * mm});
            skLineSegment(sketch, "E217.right", {"start": v(-334.07, -345.17) * mm, "end": v(-334.07, -404.2) * mm});
            skCircle(sketch, "E218", {"center": v(-277.97, -395.67) * mm, "radius": 2.05 * mm});
            skLineSegment(sketch, "E219", {"start": v(-292.02, -399.17) * mm, "end": v(-280.82, -399.17) * mm});
            skLineSegment(sketch, "E220", {"start": v(-282.55, -392.13) * mm, "end": v(-287.15, -392.13) * mm});
            skLineSegment(sketch, "E221", {"start": v(-292.02, -399.17) * mm, "end": v(-292.02, -396.68) * mm});
            skFitSpline(sketch, "E222", {"points": [v(-292.02, -396.68) * mm, v(-291.23, -394.64) * mm, v(-289.95, -393.1) * mm, v(-288.52, -392.33) * mm, v(-287.15, -392.13) * mm], "startDerivative": vector(2.38, 7.64) * mm, "endDerivative": vector(6.23, 0.5) * mm});
            skLineSegment(sketch, "E223.1.0", {"start": v(491.7, -53.31) * mm, "end": v(486.1, -43.6) * mm});
            skLineSegment(sketch, "E223.1.1", {"start": v(491.7, -53.31) * mm, "end": v(489.54, -54.56) * mm});
            skLineSegment(sketch, "E223.2.0", {"start": v(-199.68, 452.48) * mm, "end": v(-205.28, 442.78) * mm});
            skLineSegment(sketch, "E223.2.1", {"start": v(-199.68, 452.48) * mm, "end": v(-197.52, 451.23) * mm});
            skPoint(sketch, "E223.center", {"position": v(0, 0) * mm});
            skLineSegment(sketch, "E224", {"start": v(-277.88, -393.62) * mm, "end": v(-277.88, -397.71) * mm, "construction": true});
            skLineSegment(sketch, "E225", {"start": v(-280.02, -395.65) * mm, "end": v(-275.92, -395.65) * mm, "construction": true});
            skLineSegment(sketch, "E226", {"start": v(-369.4, -356) * mm, "end": v(-363.07, -356) * mm});
            skLineSegment(sketch, "E227", {"start": v(-363.07, -356) * mm, "end": v(-369.44, -384.48) * mm});
            skLineSegment(sketch, "E228", {"start": v(-369.44, -384.48) * mm, "end": v(-369.4, -356) * mm});
            skLineSegment(sketch, "E229.bottom", {"start": v(-310.13, -167.04) * mm, "end": v(-301.96, -167.04) * mm});
            skLineSegment(sketch, "E229.top", {"start": v(-310.13, -257.42) * mm, "end": v(-301.96, -257.42) * mm});
            skLineSegment(sketch, "E229.left", {"start": v(-310.13, -167.04) * mm, "end": v(-310.13, -195.12) * mm});
            skLineSegment(sketch, "E229.right", {"start": v(-301.96, -167.04) * mm, "end": v(-301.96, -257.42) * mm});
            skLineSegment(sketch, "E230.bottom", {"start": v(-310.13, -195.12) * mm, "end": v(-309.02, -195.12) * mm});
            skLineSegment(sketch, "E230.top", {"start": v(-310.13, -209.44) * mm, "end": v(-309.02, -209.44) * mm});
            skLineSegment(sketch, "E230.right", {"start": v(-309.02, -195.12) * mm, "end": v(-309.02, -209.44) * mm});
            skLineSegment(sketch, "E231.trimOffspring", {"start": v(-310.13, -209.44) * mm, "end": v(-310.13, -257.42) * mm});
            skLineSegment(sketch, "E232", {"start": v(-365.66, -187.35) * mm, "end": v(-365.66, -165.3) * mm});
            skLineSegment(sketch, "E233", {"start": v(-365.66, -165.3) * mm, "end": v(-356.92, -165.3) * mm});
            skLineSegment(sketch, "E234", {"start": v(-356.92, -165.3) * mm, "end": v(-349.99, -168.42) * mm});
            skLineSegment(sketch, "E235", {"start": v(-349.99, -168.42) * mm, "end": v(-349.99, -159.05) * mm});
            skLineSegment(sketch, "E236", {"start": v(-349.99, -159.05) * mm, "end": v(-355.26, -154.27) * mm});
            skLineSegment(sketch, "E237", {"start": v(-355.26, -154.27) * mm, "end": v(-380.7, -154.27) * mm});
            skLineSegment(sketch, "E238", {"start": v(-380.7, -154.27) * mm, "end": v(-385.63, -161.55) * mm});
            skLineSegment(sketch, "E239", {"start": v(-385.63, -161.55) * mm, "end": v(-385.63, -179.16) * mm});
            skLineSegment(sketch, "E240", {"start": v(-385.63, -179.16) * mm, "end": v(-368.57, -199.27) * mm});
            skLineSegment(sketch, "E241", {"start": v(-368.57, -199.27) * mm, "end": v(-368.57, -205.51) * mm});
            skLineSegment(sketch, "E242", {"start": v(-368.57, -205.51) * mm, "end": v(-353.94, -208.08) * mm});
            skLineSegment(sketch, "E243", {"start": v(-353.94, -208.08) * mm, "end": v(-346.73, -208.08) * mm});
            skLineSegment(sketch, "E244", {"start": v(-346.73, -208.08) * mm, "end": v(-346.73, -200.17) * mm});
            skLineSegment(sketch, "E245", {"start": v(-346.73, -200.17) * mm, "end": v(-349.7, -200.17) * mm});
            skLineSegment(sketch, "E246", {"start": v(-349.7, -200.17) * mm, "end": v(-354.7, -190.81) * mm});
            skLineSegment(sketch, "E247", {"start": v(-354.7, -190.81) * mm, "end": v(-360.73, -193.24) * mm});
            skLineSegment(sketch, "E248", {"start": v(-360.73, -193.24) * mm, "end": v(-365.66, -187.35) * mm});
            skLineSegment(sketch, "E249", {"start": v(-365.6, -312.64) * mm, "end": v(-365.6, -290.59) * mm});
            skLineSegment(sketch, "E250", {"start": v(-365.6, -290.59) * mm, "end": v(-356.86, -290.59) * mm});
            skLineSegment(sketch, "E251", {"start": v(-356.86, -290.59) * mm, "end": v(-349.93, -293.7) * mm});
            skLineSegment(sketch, "E252", {"start": v(-349.93, -293.7) * mm, "end": v(-349.93, -284.35) * mm});
            skLineSegment(sketch, "E253", {"start": v(-349.93, -284.35) * mm, "end": v(-355.2, -279.56) * mm});
            skLineSegment(sketch, "E254", {"start": v(-355.2, -279.56) * mm, "end": v(-380.65, -279.56) * mm});
            skLineSegment(sketch, "E255", {"start": v(-380.65, -279.56) * mm, "end": v(-385.57, -286.84) * mm});
            skLineSegment(sketch, "E256", {"start": v(-353.88, -333.37) * mm, "end": v(-346.67, -333.37) * mm});
            skLineSegment(sketch, "E257", {"start": v(-346.67, -333.37) * mm, "end": v(-346.67, -325.47) * mm});
            skLineSegment(sketch, "E258", {"start": v(-346.67, -325.47) * mm, "end": v(-349.65, -325.47) * mm});
            skLineSegment(sketch, "E259", {"start": v(-349.65, -325.47) * mm, "end": v(-354.64, -316.1) * mm});
            skLineSegment(sketch, "E260", {"start": v(-354.64, -316.1) * mm, "end": v(-360.67, -318.53) * mm});
            skLineSegment(sketch, "E261", {"start": v(-360.67, -318.53) * mm, "end": v(-365.6, -312.64) * mm});
            skLineSegment(sketch, "E262", {"start": v(-385.57, -286.84) * mm, "end": v(-385.57, -322.6) * mm});
            skLineSegment(sketch, "E263", {"start": v(-380.51, -328.97) * mm, "end": v(-353.88, -333.37) * mm});
            skArc(sketch, "E264", {"start": v(-385.57, -322.6) * mm, "mid": v(-384.27, -326.76) * mm, "end": v(-380.51, -328.97) * mm});
            skCircle(sketch, "E265", {"center": v(-377.32, -323.93) * mm, "radius": 2.05 * mm});
            skCircle(sketch, "E266", {"center": v(-380.7, -291.51) * mm, "radius": 2.05 * mm});
            skLineSegment(sketch, "E267", {"start": v(-47.2, -259.77) * mm, "end": v(-47.2, -275.75) * mm, "construction": true});
            skArc(sketch, "E268", {"start": v(-47.2, -259.77) * mm, "mid": v(-57.5, -264.97) * mm, "end": v(-61.61, -275.75) * mm});
            skLineSegment(sketch, "E269", {"start": v(-47.2, -259.77) * mm, "end": v(-28.4, -259.77) * mm});
            skLineSegment(sketch, "E270", {"start": v(-42.06, -267.32) * mm, "end": v(-20.98, -267.32) * mm});
            skLineSegment(sketch, "E271", {"start": v(-41.22, -275.75) * mm, "end": v(-42.06, -275.75) * mm, "construction": true});
            skPoint(sketch, "E272.end.orphan", {"position": v(-20.98, -284.17) * mm});
            skPoint(sketch, "E273.end.orphan", {"position": v(-28.4, -291.6) * mm});
            skLineSegment(sketch, "E274.trimOffspring", {"start": v(-47.2, -275.75) * mm, "end": v(-61.61, -275.75) * mm, "construction": true});
            skArc(sketch, "E275", {"start": v(-42.06, -267.32) * mm, "mid": v(-47.72, -269.85) * mm, "end": v(-49.62, -275.75) * mm});
            skFitSpline(sketch, "E276", {"points": [v(-20.98, -267.32) * mm, v(-20.07, -267.37) * mm, v(-19.16, -267.5) * mm, v(-17.94, -267.9) * mm, v(-16.6, -268.6) * mm], "startDerivative": vector(4.12, -0.12) * mm, "endDerivative": vector(4.64, -2.63) * mm});
            skFitSpline(sketch, "E277", {"points": [v(-28.4, -259.77) * mm, v(-27.12, -259.77) * mm, v(-24.76, -260.2) * mm, v(-21.23, -261.69) * mm, v(-18.74, -263.37) * mm, v(-16.6, -265.68) * mm], "startDerivative": vector(8.63, 0.33) * mm, "endDerivative": vector(9.61, -11.26) * mm});
            skLineSegment(sketch, "E278", {"start": v(-16.6, -265.68) * mm, "end": v(-16.6, -268.6) * mm});
            skArc(sketch, "E279.MirrorCS", {"start": v(-47.2, -291.73) * mm, "mid": v(-57.5, -286.53) * mm, "end": v(-61.61, -275.75) * mm});
            skLineSegment(sketch, "E280.MirrorCS", {"start": v(-47.2, -291.73) * mm, "end": v(-28.4, -291.73) * mm});
            skLineSegment(sketch, "E281.MirrorCS", {"start": v(-42.06, -284.17) * mm, "end": v(-20.98, -284.17) * mm});
            skArc(sketch, "E282.MirrorCS", {"start": v(-42.06, -284.17) * mm, "mid": v(-47.72, -281.65) * mm, "end": v(-49.62, -275.75) * mm});
            skFitSpline(sketch, "E283.MirrorCS", {"points": [v(-28.4, -291.73) * mm, v(-27.12, -291.73) * mm, v(-24.76, -291.3) * mm, v(-21.23, -289.8) * mm, v(-18.74, -288.13) * mm, v(-16.6, -285.82) * mm], "startDerivative": vector(8.63, -0.33) * mm, "endDerivative": vector(9.61, 11.26) * mm});
            skLineSegment(sketch, "E284.MirrorCS", {"start": v(-16.6, -285.82) * mm, "end": v(-16.6, -282.9) * mm});
            skFitSpline(sketch, "E285.MirrorCS", {"points": [v(-20.98, -284.17) * mm, v(-20.07, -284.13) * mm, v(-19.16, -284) * mm, v(-17.94, -283.6) * mm, v(-16.6, -282.9) * mm], "startDerivative": vector(4.12, 0.12) * mm, "endDerivative": vector(4.64, 2.63) * mm});
            skLineSegment(sketch, "E286", {"start": v(-79.87, -160.28) * mm, "end": v(-79.87, -181.47) * mm, "construction": true});
            skFitSpline(sketch, "E287", {"points": [v(-89.87, -160.96) * mm, v(-79.87, -160.28) * mm, v(-69.87, -160.9) * mm], "startDerivative": vector(20, 2.02) * mm, "endDerivative": vector(20.1, -1.88) * mm});
            skLineSegment(sketch, "E288", {"start": v(-89.87, -160.96) * mm, "end": v(-89.87, -162.7) * mm});
            skLineSegment(sketch, "E289", {"start": v(-69.87, -162.7) * mm, "end": v(-69.87, -160.9) * mm});
            skLineSegment(sketch, "E290", {"start": v(-81.86, -170.99) * mm, "end": v(-79.87, -170.99) * mm, "construction": true});
            skArc(sketch, "E291", {"start": v(-81.86, -170.99) * mm, "mid": v(-84.19, -165.22) * mm, "end": v(-89.87, -162.7) * mm});
            skPoint(sketch, "E292.orphan", {"position": v(-89.87, -179.26) * mm});
            skArc(sketch, "E293.MirrorCS", {"start": v(-77.87, -170.99) * mm, "mid": v(-75.55, -165.22) * mm, "end": v(-69.87, -162.7) * mm});
            skArc(sketch, "E294.MirrorCS", {"start": v(-81.86, -170.99) * mm, "mid": v(-84.19, -176.76) * mm, "end": v(-89.87, -179.28) * mm});
            skFitSpline(sketch, "E295.MirrorCS", {"points": [v(-89.87, -181.02) * mm, v(-79.87, -181.7) * mm, v(-69.87, -181.09) * mm], "startDerivative": vector(20, -2.02) * mm, "endDerivative": vector(20.1, 1.88) * mm});
            skLineSegment(sketch, "E296.MirrorCS", {"start": v(-89.87, -181.02) * mm, "end": v(-89.87, -179.28) * mm});
            skArc(sketch, "E297.MirrorCS", {"start": v(-77.87, -170.99) * mm, "mid": v(-75.55, -176.76) * mm, "end": v(-69.87, -179.28) * mm});
            skLineSegment(sketch, "E298.MirrorCS", {"start": v(-69.87, -179.28) * mm, "end": v(-69.87, -181.09) * mm});
            skFitSpline(sketch, "E299", {"points": [v(-112.28, -325.05) * mm, v(-108.99, -323.48) * mm, v(-105.58, -322.93) * mm, v(-102.55, -322.93) * mm, v(-98.79, -323.8) * mm, v(-95.87, -325.4) * mm, v(-93.4, -327.5) * mm, v(-91.67, -329.86) * mm], "startDerivative": vector(21.55, 12.19) * mm, "endDerivative": vector(11.77, -18.25) * mm});
            skLineSegment(sketch, "E300", {"start": v(-91.67, -329.86) * mm, "end": v(-95.32, -335.32) * mm});
            skLineSegment(sketch, "E301", {"start": v(-95.32, -335.32) * mm, "end": v(-91.95, -337.56) * mm});
            skLineSegment(sketch, "E302", {"start": v(-91.95, -337.56) * mm, "end": v(-90.89, -335.97) * mm});
            skLineSegment(sketch, "E303", {"start": v(-90.89, -335.97) * mm, "end": v(-87.05, -338.53) * mm});
            skLineSegment(sketch, "E304", {"start": v(-87.05, -338.53) * mm, "end": v(-87.05, -343.77) * mm});
            skLineSegment(sketch, "E305", {"start": v(-87.05, -343.77) * mm, "end": v(-91.4, -349.78) * mm});
            skLineSegment(sketch, "E306", {"start": v(-112.28, -325.05) * mm, "end": v(-112.51, -333.86) * mm});
            skFitSpline(sketch, "E307", {"points": [v(-112.51, -333.86) * mm, v(-115.29, -338.16) * mm, v(-117.44, -341.25) * mm, v(-120.05, -344.06) * mm, v(-123.1, -346.3) * mm, v(-125.53, -347.52) * mm, v(-128.77, -347.97) * mm, v(-131.29, -347.85) * mm, v(-134.55, -346.78) * mm, v(-136.24, -345.82) * mm, v(-138.13, -344.64) * mm, v(-139.4, -343.76) * mm], "startDerivative": vector(-24.33, -37.91) * mm, "endDerivative": vector(-18.08, 13.1) * mm});
            skFitSpline(sketch, "E308", {"points": [v(-139.4, -343.76) * mm, v(-139.97, -343.64) * mm, v(-140.99, -343.76) * mm, v(-142.03, -344.63) * mm, v(-142.38, -345.52) * mm, v(-142.4, -346.48) * mm, v(-141.2, -348.07) * mm, v(-137.38, -350.34) * mm, v(-134.07, -351.76) * mm, v(-129.94, -352.75) * mm, v(-125.71, -353.25) * mm, v(-121.95, -353.25) * mm, v(-120.6, -352.84) * mm, v(-119.12, -351.55) * mm, v(-117.15, -349.87) * mm, v(-114.3, -348.2) * mm, v(-111.15, -346.89) * mm, v(-107.23, -346.1) * mm, v(-104.46, -345.9) * mm, v(-100.49, -346.13) * mm, v(-97.32, -346.94) * mm, v(-95.25, -347.69) * mm, v(-91.4, -349.78) * mm], "startDerivative": vector(-24.23, 6.5) * mm, "endDerivative": vector(70.38, -40.72) * mm});
            skLineSegment(sketch, "E309", {"start": v(-178.6, -295.26) * mm, "end": v(-148.26, -267.96) * mm});
            skLineSegment(sketch, "E310", {"start": v(-172.74, -300.43) * mm, "end": v(-174.23, -305.3) * mm});
            skLineSegment(sketch, "E311", {"start": v(-159.3, -308.5) * mm, "end": v(-150.67, -293.52) * mm});
            skLineSegment(sketch, "E312", {"start": v(-150.67, -293.52) * mm, "end": v(-136.97, -306.93) * mm});
            skLineSegment(sketch, "E313", {"start": v(-126.3, -293.46) * mm, "end": v(-129.68, -293.46) * mm});
            skLineSegment(sketch, "E314", {"start": v(-129.68, -293.46) * mm, "end": v(-140.23, -274.98) * mm});
            skLineSegment(sketch, "E315", {"start": v(-178.6, -295.26) * mm, "end": v(-172.74, -300.43) * mm});
            skFitSpline(sketch, "E316", {"points": [v(-136.97, -306.93) * mm, v(-135.6, -307.76) * mm, v(-133.41, -308.44) * mm, v(-126.3, -308.39) * mm], "startDerivative": vector(5.72, -3.74) * mm, "endDerivative": vector(16.58, 0.87) * mm});
            skFitSpline(sketch, "E317", {"points": [v(-126.3, -308.39) * mm, v(-124.2, -306.2) * mm, v(-122.07, -304.28) * mm, v(-119.94, -303.23) * mm, v(-117.22, -302.57) * mm, v(-114.05, -301.46) * mm, v(-111.16, -299.18) * mm, v(-108.83, -296.53) * mm, v(-107.73, -293.7) * mm, v(-107.74, -292.89) * mm, v(-108, -292.05) * mm, v(-108.51, -291.53) * mm, v(-109.14, -291.25) * mm, v(-110.08, -291.26) * mm, v(-110.72, -291.36) * mm, v(-111.53, -291.9) * mm, v(-112, -292.74) * mm, v(-113.34, -294.48) * mm, v(-114.52, -295.81) * mm, v(-116.69, -296.76) * mm, v(-119.09, -297.12) * mm, v(-121.57, -296.9) * mm, v(-123.68, -296.16) * mm, v(-125.1, -294.99) * mm, v(-126.3, -293.46) * mm], "startDerivative": vector(39.35, 41.88) * mm, "endDerivative": vector(-27.48, 37.58) * mm});
            skFitSpline(sketch, "E318", {"points": [v(-148.26, -267.96) * mm, v(-146.9, -268.48) * mm, v(-145.41, -269.57) * mm, v(-141.77, -272.86) * mm, v(-140.23, -274.98) * mm], "startDerivative": vector(7.52, -2.37) * mm, "endDerivative": vector(4.78, -7.82) * mm});
            skFitSpline(sketch, "E319", {"points": [v(-174.23, -305.3) * mm, v(-172.54, -306.67) * mm, v(-169.92, -308.35) * mm, v(-167.06, -309.74) * mm, v(-164.27, -310.8) * mm, v(-162.63, -311.24) * mm, v(-161.83, -311.33) * mm, v(-161.22, -311.23) * mm, v(-160.74, -311) * mm, v(-160.2, -310.3) * mm, v(-159.3, -308.5) * mm], "startDerivative": vector(13.7, -11.7) * mm, "endDerivative": vector(8.42, 17.97) * mm});
            skLineSegment(sketch, "E320.MirrorCS", {"start": v(-120.54, -229.01) * mm, "end": v(-123.92, -229.01) * mm});
            skLineSegment(sketch, "E321.MirrorCS", {"start": v(-166.98, -222.05) * mm, "end": v(-168.47, -217.18) * mm});
            skFitSpline(sketch, "E322.MirrorCS", {"points": [v(-168.47, -217.18) * mm, v(-166.78, -215.8) * mm, v(-164.16, -214.13) * mm, v(-161.3, -212.74) * mm, v(-158.51, -211.68) * mm, v(-156.87, -211.23) * mm, v(-156.07, -211.15) * mm, v(-155.46, -211.25) * mm, v(-154.98, -211.48) * mm, v(-154.44, -212.17) * mm, v(-153.54, -213.97) * mm], "startDerivative": vector(13.7, 11.7) * mm, "endDerivative": vector(8.42, -17.97) * mm});
            skFitSpline(sketch, "E323.MirrorCS", {"points": [v(-120.54, -214.09) * mm, v(-118.44, -216.28) * mm, v(-116.31, -218.2) * mm, v(-114.18, -219.25) * mm, v(-111.46, -219.91) * mm, v(-108.3, -221.01) * mm, v(-105.4, -223.3) * mm, v(-103.07, -225.94) * mm, v(-101.97, -228.79) * mm, v(-101.98, -229.59) * mm, v(-102.24, -230.42) * mm, v(-102.75, -230.95) * mm, v(-103.38, -231.23) * mm, v(-104.32, -231.22) * mm, v(-104.96, -231.12) * mm, v(-105.77, -230.58) * mm, v(-106.25, -229.73) * mm, v(-107.58, -228) * mm, v(-108.76, -226.66) * mm, v(-110.93, -225.71) * mm, v(-113.33, -225.35) * mm, v(-115.81, -225.57) * mm, v(-117.92, -226.31) * mm, v(-119.34, -227.49) * mm, v(-120.54, -229.01) * mm], "startDerivative": vector(39.35, -41.88) * mm, "endDerivative": vector(-27.48, -37.58) * mm});
            skFitSpline(sketch, "E324.MirrorCS", {"points": [v(-131.2, -215.54) * mm, v(-129.84, -214.71) * mm, v(-127.65, -214.03) * mm, v(-120.54, -214.09) * mm], "startDerivative": vector(5.72, 3.74) * mm, "endDerivative": vector(16.58, -0.87) * mm});
            skFitSpline(sketch, "E325.MirrorCS", {"points": [v(-142.5, -254.52) * mm, v(-141.14, -254) * mm, v(-139.65, -252.9) * mm, v(-136.01, -249.61) * mm, v(-134.47, -247.5) * mm], "startDerivative": vector(7.52, 2.37) * mm, "endDerivative": vector(4.78, 7.82) * mm});
            skLineSegment(sketch, "E326.MirrorCS", {"start": v(-172.85, -227.22) * mm, "end": v(-166.98, -222.05) * mm});
            skLineSegment(sketch, "E327.MirrorCS", {"start": v(-144.91, -228.96) * mm, "end": v(-131.2, -215.54) * mm});
            skLineSegment(sketch, "E328.MirrorCS", {"start": v(-172.85, -227.22) * mm, "end": v(-163.57, -235.57) * mm});
            skLineSegment(sketch, "E329.MirrorCS", {"start": v(-123.92, -229.01) * mm, "end": v(-134.47, -247.5) * mm});
            skLineSegment(sketch, "E330.MirrorCS", {"start": v(-153.54, -213.97) * mm, "end": v(-144.91, -228.96) * mm});
            skLineSegment(sketch, "E331", {"start": v(-163.57, -235.57) * mm, "end": v(-165.9, -238.17) * mm});
            skLineSegment(sketch, "E332", {"start": v(-170.37, -236.15) * mm, "end": v(-176.35, -235.95) * mm});
            skArc(sketch, "E333", {"start": v(-170.37, -236.15) * mm, "mid": v(-168.87, -238.8) * mm, "end": v(-165.9, -238.17) * mm});
            skArc(sketch, "E334", {"start": v(-176.35, -235.95) * mm, "mid": v(-164.5, -254.49) * mm, "end": v(-142.5, -254.52) * mm});
            skLineSegment(sketch, "E335", {"start": v(-162.7, 40.87) * mm, "end": v(-159.05, 13.52) * mm});
            skLineSegment(sketch, "E336", {"start": v(-145, 15.4) * mm, "end": v(-148.72, 42.74) * mm});
            skArc(sketch, "E337", {"start": v(-159.05, 13.52) * mm, "mid": v(-151.09, 7.41) * mm, "end": v(-145, 15.4) * mm});
            skSolve(sketch);
        }
        {
            var Q0;
            Q0 = qSketchRegion(id + "F0", true);
            extrude(context, id + "F1", {"entities" : qUnion([Q0]), "depth" : 4 * mm, "offsetDistance" : 25 * mm});
        }
    });
